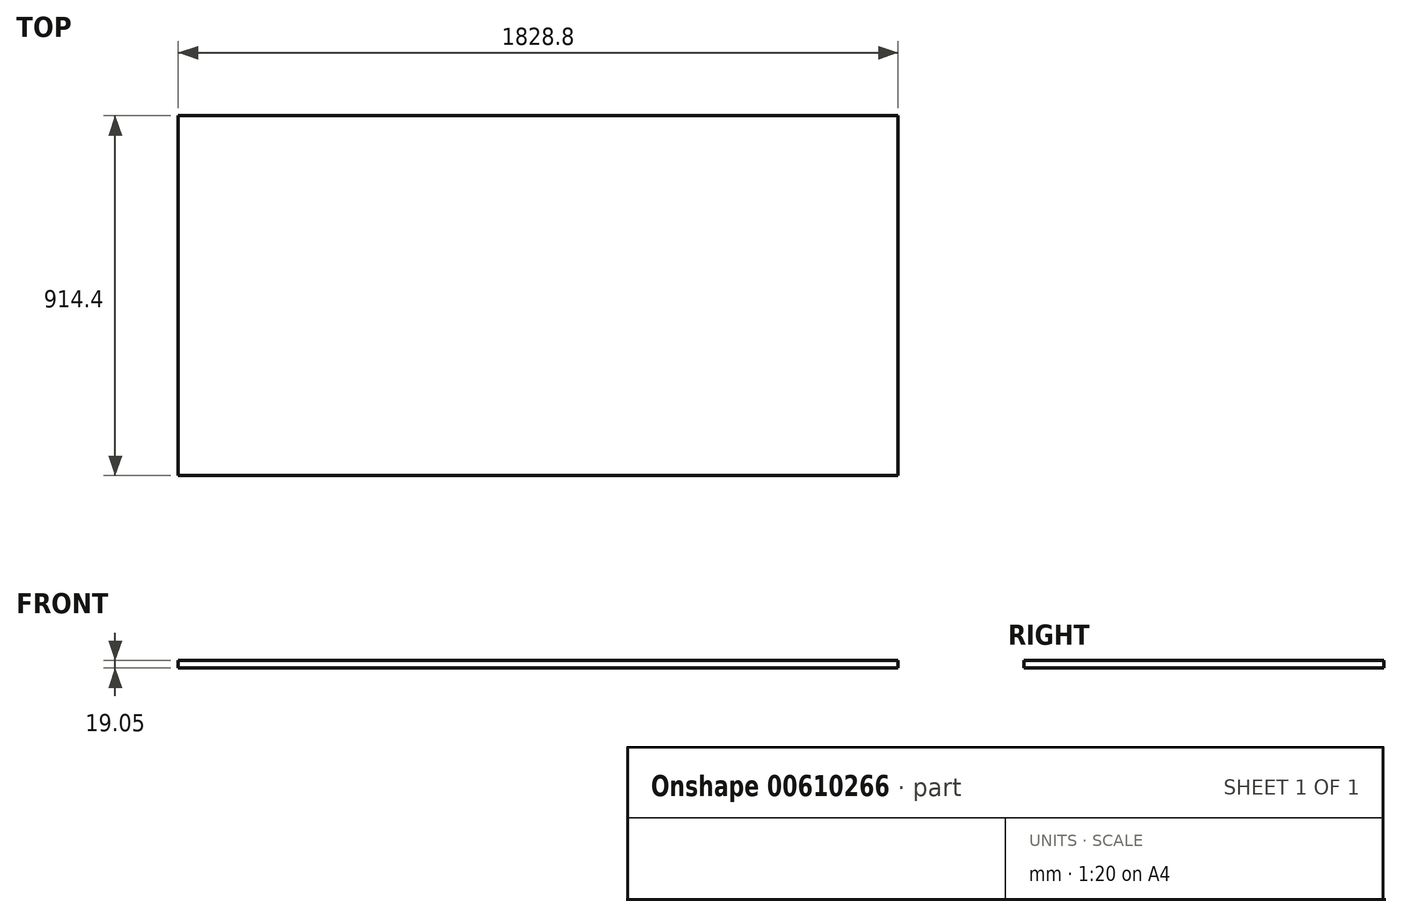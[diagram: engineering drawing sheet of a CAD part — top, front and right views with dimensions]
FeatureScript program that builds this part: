
annotation { "Feature Type Name" : "Feature", "Feature Type Description" : "" }
export const myFeature = defineFeature(function(context is Context, id is Id, definition is map)
    precondition{}
    {
        {
            var Q0;
            Q0=qCreatedBy(makeId("Top.planeOp"),FACE);
            var sketch = newSketch(context, id + "F0", { "sketchPlane" : qUnion([Q0])});
            skLineSegment(sketch, "E0.bottom", {"start": v(-914.4, 457.2) * mm, "end": v(914.4, 457.2) * mm});
            skLineSegment(sketch, "E0.top", {"start": v(-914.4, -457.2) * mm, "end": v(914.4, -457.2) * mm});
            skLineSegment(sketch, "E0.left", {"start": v(-914.4, 457.2) * mm, "end": v(-914.4, -457.2) * mm});
            skLineSegment(sketch, "E0.right", {"start": v(914.4, 457.2) * mm, "end": v(914.4, -457.2) * mm});
            skSolve(sketch);
        }
        {
            var Q0;
            Q0 = qSketchRegion(id + "F0", true);
            extrude(context, id + "F1", {"entities" : qUnion([Q0]), "depth" : 19.05 * mm, "offsetDistance" : 25.4 * mm});
        }
    });
